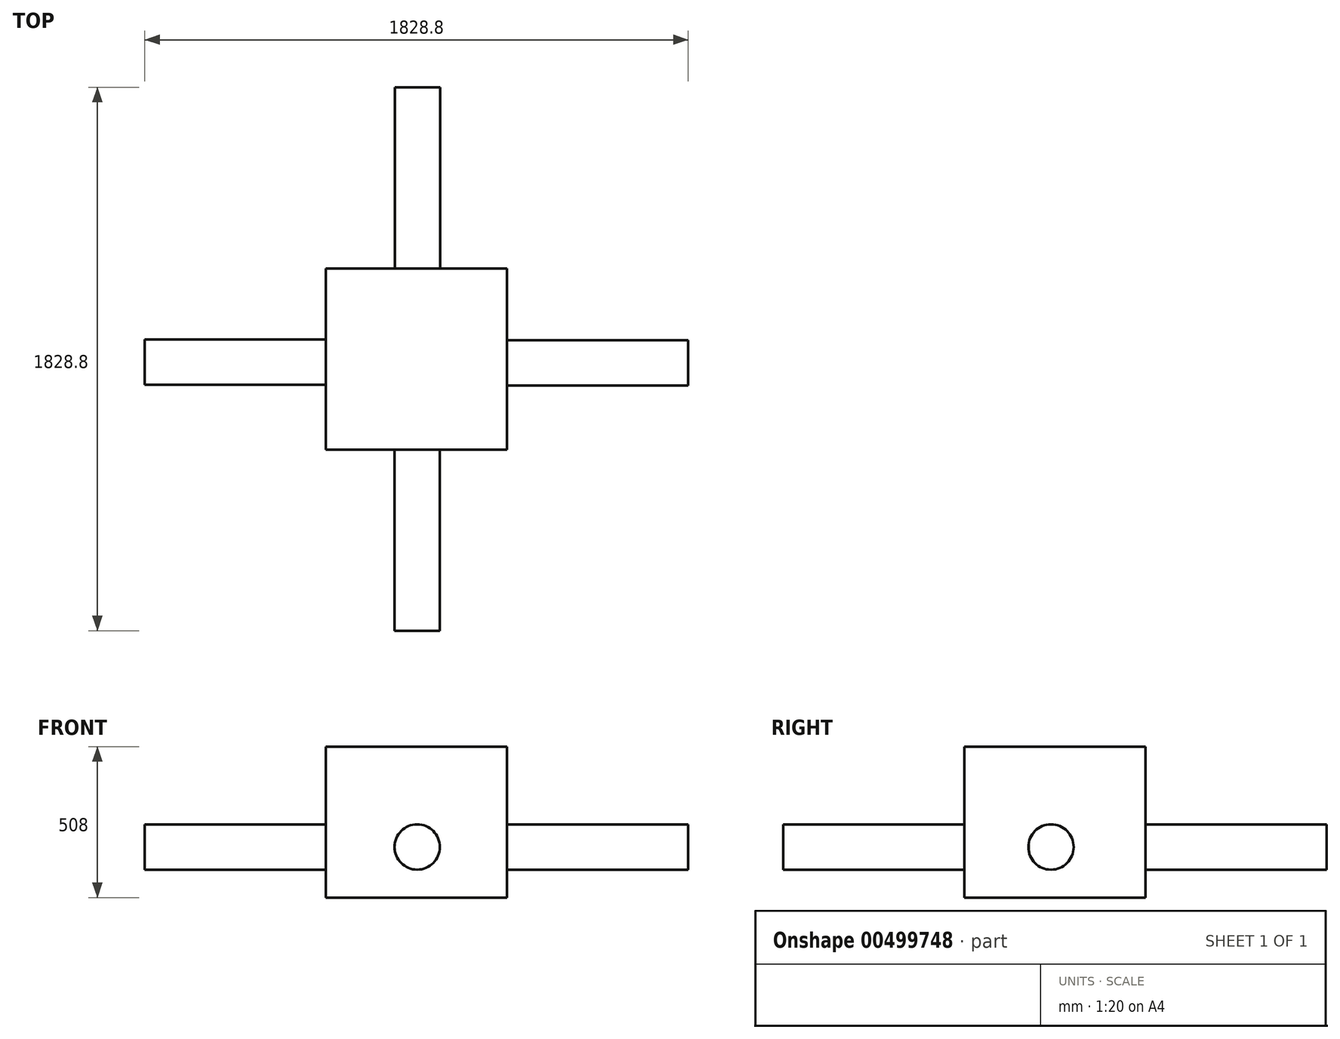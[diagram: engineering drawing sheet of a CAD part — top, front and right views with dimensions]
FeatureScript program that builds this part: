
annotation { "Feature Type Name" : "Feature", "Feature Type Description" : "" }
export const myFeature = defineFeature(function(context is Context, id is Id, definition is map)
    precondition{}
    {
        {
            var Q0;
            Q0=qCreatedBy(makeId("Top.planeOp"),FACE);
            var sketch = newSketch(context, id + "F0", { "sketchPlane" : qUnion([Q0])});
            skLineSegment(sketch, "E0.bottom", {"start": v(-97.57, -110.49) * mm, "end": v(512.03, -110.49) * mm});
            skLineSegment(sketch, "E0.top", {"start": v(-97.57, 499.11) * mm, "end": v(512.03, 499.11) * mm});
            skLineSegment(sketch, "E0.left", {"start": v(-97.57, -110.49) * mm, "end": v(-97.57, 499.11) * mm});
            skLineSegment(sketch, "E0.right", {"start": v(512.03, -110.49) * mm, "end": v(512.03, 499.11) * mm});
            skSolve(sketch);
        }
        {
            var Q0;
            Q0=makeQuery(id+"F0.imprint","IMPRINT",FACE,{"disambiguationData":[TD([[makeQuery(id+"F0.imprint","IMPRINT",EDGE,{"derivedFrom":sQuery(id+"F0.wireOp",EDGE,"E0.bottom")}),1.0]])]});
            extrude(context, id + "F1", {"entities" : qUnion([Q0]), "depth" : 508 * mm});
        }
        {
            var Q0;
            Q0=makeQuery(id+"F1.opExtrude","SWEPT_FACE",FACE,{"disambiguationData":[OSD([sQuery(id+"F0.wireOp",EDGE,"E0.bottom")])]});
            var sketch = newSketch(context, id + "F2", { "sketchPlane" : qUnion([Q0])});
            skCircle(sketch, "E1", {"center": v(209.3, 170.04) * mm, "radius": 76.2 * mm});
            skSolve(sketch);
        }
        {
            var Q0;
            Q0=makeQuery(id+"F2.imprint","IMPRINT",FACE,{"disambiguationData":[TD([[makeQuery(id+"F2.imprint","IMPRINT",EDGE,{"derivedFrom":sQuery(id+"F2.wireOp",EDGE,"E1")}),1.0]])]});
            extrude(context, id + "F3", {"entities" : qUnion([Q0]), "operationType" : NewBodyOperationType.ADD, "depth" : 609.6 * mm});
        }
        {
            var Q0;
            Q0=makeQuery(id+"F1.opExtrude","SWEPT_FACE",FACE,{"disambiguationData":[OSD([sQuery(id+"F0.wireOp",EDGE,"E0.left")])]});
            var sketch = newSketch(context, id + "F4", { "sketchPlane" : qUnion([Q0])});
            skCircle(sketch, "E2", {"center": v(-183.06, 169.94) * mm, "radius": 76.2 * mm});
            skSolve(sketch);
        }
        {
            var Q0;
            Q0=makeQuery(id+"F4.imprint","IMPRINT",FACE,{"disambiguationData":[TD([[makeQuery(id+"F4.imprint","IMPRINT",EDGE,{"derivedFrom":sQuery(id+"F4.wireOp",EDGE,"E2")}),1.0]])]});
            extrude(context, id + "F5", {"entities" : qUnion([Q0]), "operationType" : NewBodyOperationType.ADD, "depth" : 609.6 * mm});
        }
        {
            var Q0;
            Q0=makeQuery(id+"F1.opExtrude","SWEPT_FACE",FACE,{"disambiguationData":[OSD([sQuery(id+"F0.wireOp",EDGE,"E0.top")])]});
            var sketch = newSketch(context, id + "F6", { "sketchPlane" : qUnion([Q0])});
            skCircle(sketch, "E3", {"center": v(-210.82, 169.94) * mm, "radius": 76.2 * mm});
            skSolve(sketch);
        }
        {
            var Q0;
            Q0=makeQuery(id+"F6.imprint","IMPRINT",FACE,{"disambiguationData":[TD([[makeQuery(id+"F6.imprint","IMPRINT",EDGE,{"derivedFrom":sQuery(id+"F6.wireOp",EDGE,"E3")}),1.0]])]});
            extrude(context, id + "F7", {"entities" : qUnion([Q0]), "operationType" : NewBodyOperationType.ADD, "depth" : 609.6 * mm});
        }
        {
            var Q0;
            Q0=makeQuery(id+"F1.opExtrude","SWEPT_FACE",FACE,{"disambiguationData":[OSD([sQuery(id+"F0.wireOp",EDGE,"E0.right")])]});
            var sketch = newSketch(context, id + "F8", { "sketchPlane" : qUnion([Q0])});
            skCircle(sketch, "E4", {"center": v(180.43, 169.94) * mm, "radius": 76.2 * mm});
            skSolve(sketch);
        }
        {
            var Q0;
            Q0=makeQuery(id+"F8.imprint","IMPRINT",FACE,{"disambiguationData":[TD([[makeQuery(id+"F8.imprint","IMPRINT",EDGE,{"derivedFrom":sQuery(id+"F8.wireOp",EDGE,"E4")}),1.0]])]});
            extrude(context, id + "F9", {"entities" : qUnion([Q0]), "operationType" : NewBodyOperationType.ADD, "depth" : 609.6 * mm});
        }
    });
